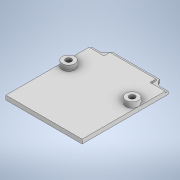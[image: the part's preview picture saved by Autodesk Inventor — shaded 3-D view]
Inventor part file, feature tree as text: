
AUTODESK INVENTOR PART (.ipt)
format: ipt  version: 2022 (Build 260153000, 153)  size: 174,592 bytes
history: native  units: mm
features: extrude x6, sketch x6
ambient origin geometry x8: Origin, YZ Plane, XZ Plane, XY Plane, X Axis, Y Axis, Z Axis, Center Point
bodies: Solid1 (feature_tree)
feature tree (12):
  extrude  "Extrusion1"  Depth=3.4mm TaperAngle=0.0deg
  extrude  "Extrusion2"  Depth=3.4mm TaperAngle=0.0deg
  extrude  "Extrusion3"  Depth=2.051mm TaperAngle=0.0deg
  extrude  "Extrusion4"  Depth=10.0mm TaperAngle=0.0deg
  extrude  "Extrusion11"  [1 undecoded]
  extrude  "Extrusion12"  [1 undecoded]
  sketch  "Sketch1"  dims[d0=1.5mm d1=0.0mm d2=3.4mm d3=0.0mm]
  sketch  "Sketch2"  dims[d4=2.032mm d5=3.4mm d6=0.0mm]
  sketch  "Sketch3"  dims[d7=4.064mm d8=4.064mm d9=2.051mm d10=0.0mm]
  sketch  "Sketch4"  dims[d40=6.7mm d54=10.0mm d55=0.0mm]
  sketch  "Sketch13"  dims[d56=0.5mm d57=0.0mm]
  sketch  "Sketch14"
note: 2 required parameter values undecoded (feature->parameter linkage not recoverable at this tier; creation-order binding heuristic only, values carry confidence <= 0.55)
